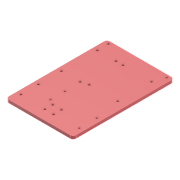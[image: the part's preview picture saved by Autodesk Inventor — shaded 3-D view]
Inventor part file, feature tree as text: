
AUTODESK INVENTOR PART (.ipt)
format: ipt  version: 2022 (Build 260153000, 153)  size: 241,152 bytes
history: native  units: mm
features: hole x5, sketch x4, extrude x2, fillet x1
ambient origin geometry x8: Origin, YZ Plane, XZ Plane, XY Plane, X Axis, Y Axis, Z Axis, Center Point
bodies: Solid1 (feature_tree)
feature tree (12):
  extrude  "Base"  TaperAngle=0.0deg  [1 undecoded]
  hole  "Mounting Holes"  [1 undecoded]
  fillet  "Fillet1"  Radius=50.0mm
  hole  "RasPi Mounting Holes"  [1 undecoded]
  hole  "LM2596 Mounting Holes"  [1 undecoded]
  hole  "Camera Mount Mounting Holes"  [1 undecoded]
  extrude  "SP RITE Logo"  Depth=30.0mm
  hole  "Button Board Mounting Holes"  [1 undecoded]
  sketch  "Sketch11"  dims[d2=115.0mm d4=0.0mm]
  sketch  "Sketch15"  dims[d21=5.0mm d91=18.0mm d92=50.0mm]
  sketch  "Sketch16"  dims[d93=5.0mm d94=50.0mm]
  sketch  "Sketch18"  dims[d95=3.4mm d96=6.0mm d97=4.0mm d98=2.0mm d99=90.0deg d100=6.0mm d101=0.0mm d104=58.0mm d105=3.4mm d106=6.0mm d107=4.0mm d108=2.0mm d109=90.0deg d110=6.0mm d111=0.0mm d112=40.0mm d113=30.0mm d122=32.0mm d123=61.5mm d125=3.4mm d126=6.0mm d127=4.0mm d128=2.0mm d129=90.0deg d130=6.0mm d131=0.0mm d132=15.0mm d133=13.5mm d135=3.4mm d136=6.0mm d137=4.0mm d138=2.0mm d139=90.0deg d140=6.0mm d141=0.0mm d223=2.0mm d224=0.0mm d263=24.0mm d264=16.5mm d266=49.0mm d267=7.0mm d273=3.0mm d274=6.0mm d275=4.0mm d276=2.0mm d277=90.0deg d278=8.0mm d279=20.594885mm d281=40.6mm d282=12.2mm d284=12.2mm d285=33.1mm d240=0.5mm d241=0.872665mm d242=0.5mm d243=0.872665mm]
note: 6 required parameter values undecoded (feature->parameter linkage not recoverable at this tier; creation-order binding heuristic only, values carry confidence <= 0.55)
